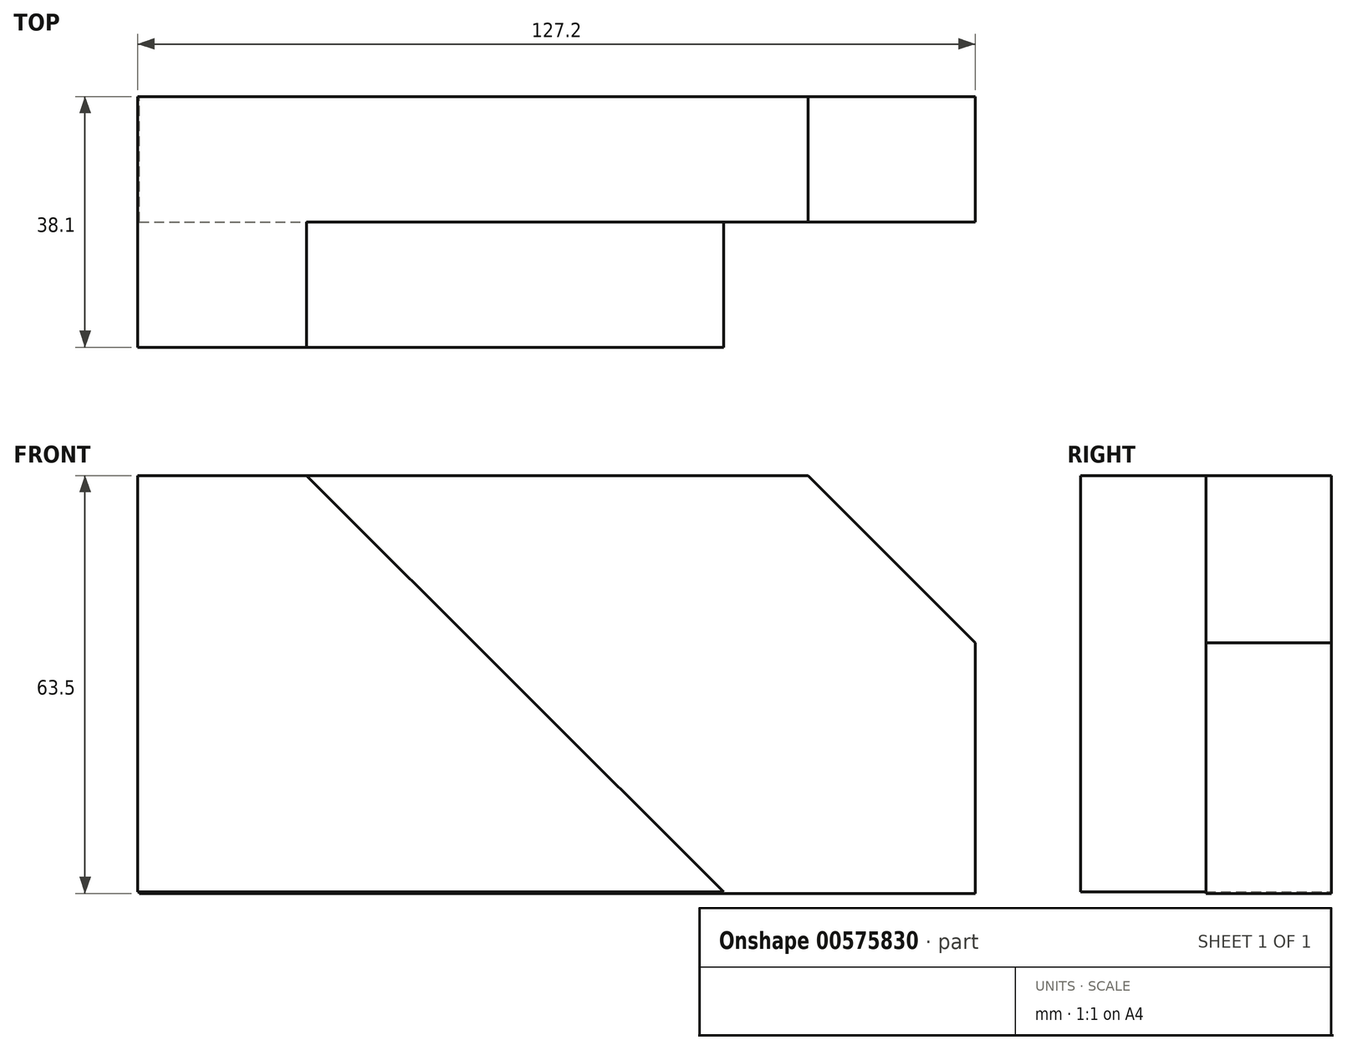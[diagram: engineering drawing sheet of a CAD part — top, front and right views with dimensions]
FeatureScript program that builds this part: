
annotation { "Feature Type Name" : "Feature", "Feature Type Description" : "" }
export const myFeature = defineFeature(function(context is Context, id is Id, definition is map)
    precondition{}
    {
        {
            var Q0;
            Q0=qCreatedBy(makeId("Front.planeOp"),FACE);
            var sketch = newSketch(context, id + "F0", { "sketchPlane" : qUnion([Q0])});
            skLineSegment(sketch, "E0", {"start": v(-76, 0) * mm, "end": v(-76, -63.5) * mm});
            skLineSegment(sketch, "E1", {"start": v(-76, -63.5) * mm, "end": v(51, -63.5) * mm});
            skLineSegment(sketch, "E2", {"start": v(51, -63.5) * mm, "end": v(51, -25.4) * mm});
            skLineSegment(sketch, "E3", {"start": v(25.6, 0) * mm, "end": v(-76, 0) * mm});
            skLineSegment(sketch, "E4", {"start": v(25.6, 0) * mm, "end": v(51, -25.4) * mm});
            skPoint(sketch, "E5.orphan", {"position": v(51, 0) * mm});
            skSolve(sketch);
        }
        {
            var Q0;
            Q0 = qSketchRegion(id + "F0", true);
            extrude(context, id + "F1", {"entities" : qUnion([Q0]), "depth" : 19.05 * mm, "offsetDistance" : 25.4 * mm});
        }
        {
            var Q0;
            Q0=qCreatedBy(makeId("Front.planeOp"),FACE);
            var sketch = newSketch(context, id + "F2", { "sketchPlane" : qUnion([Q0])});
            skLineSegment(sketch, "E6", {"start": v(-76.2, 0) * mm, "end": v(-50.6, 0) * mm});
            skLineSegment(sketch, "E7", {"start": v(12.8, -63.25) * mm, "end": v(-50.6, 0) * mm});
            skLineSegment(sketch, "E8", {"start": v(12.8, -63.25) * mm, "end": v(-76.2, -63.25) * mm});
            skLineSegment(sketch, "E9", {"start": v(-76.2, -63.25) * mm, "end": v(-76.2, 0) * mm});
            skSolve(sketch);
        }
        {
            var Q0;
            Q0 = qSketchRegion(id + "F2", true);
            extrude(context, id + "F3", {"entities" : qUnion([Q0]), "operationType" : NewBodyOperationType.ADD, "depth" : 38.1 * mm, "offsetDistance" : 25.4 * mm});
        }
    });
